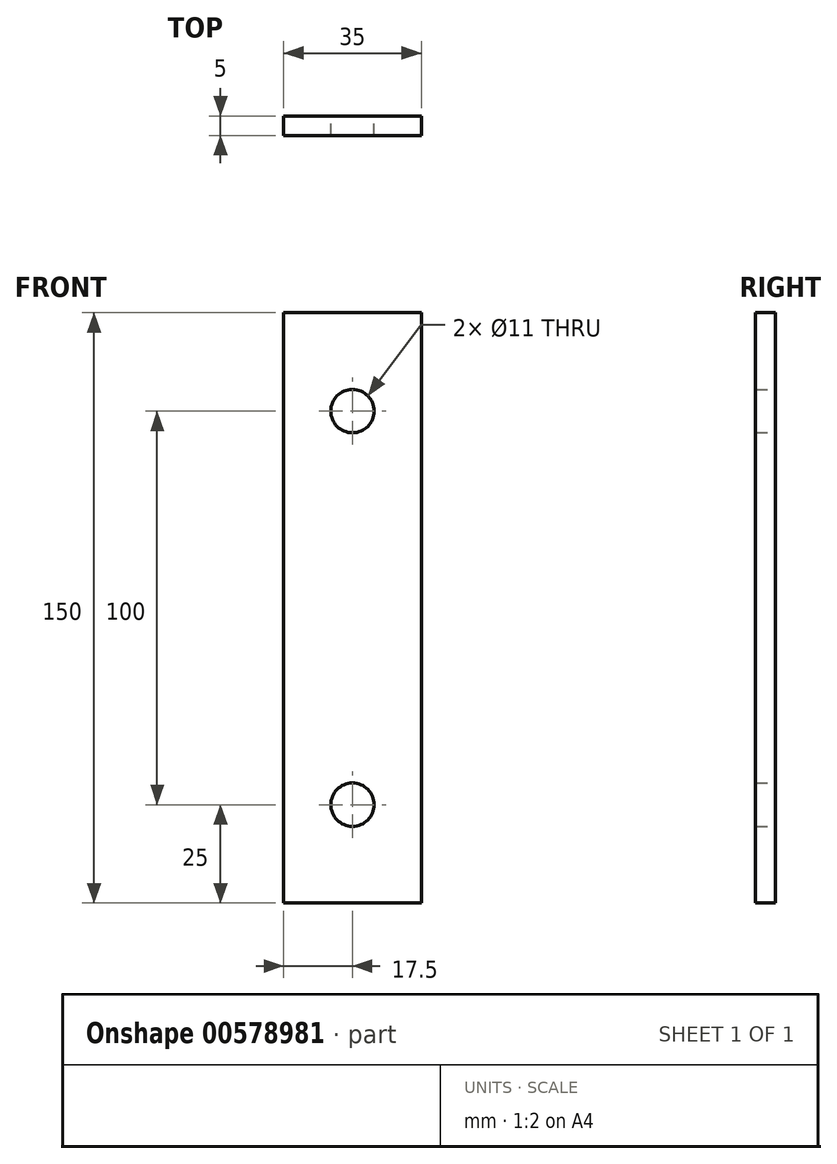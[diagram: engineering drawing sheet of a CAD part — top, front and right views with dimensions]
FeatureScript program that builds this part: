
annotation { "Feature Type Name" : "Feature", "Feature Type Description" : "" }
export const myFeature = defineFeature(function(context is Context, id is Id, definition is map)
    precondition{}
    {
        {
            var Q0;
            Q0=qCreatedBy(makeId("Front.planeOp"),FACE);
            var sketch = newSketch(context, id + "F0", { "sketchPlane" : qUnion([Q0])});
            skLineSegment(sketch, "E0.bottom", {"start": v(17.5, 75) * mm, "end": v(-17.5, 75) * mm});
            skLineSegment(sketch, "E0.top", {"start": v(17.5, -75) * mm, "end": v(-17.5, -75) * mm});
            skLineSegment(sketch, "E0.left", {"start": v(17.5, 75) * mm, "end": v(17.5, -75) * mm});
            skLineSegment(sketch, "E0.right", {"start": v(-17.5, 75) * mm, "end": v(-17.5, -75) * mm});
            skPoint(sketch, "E0.middle", {"position": v(0, 0) * mm});
            skCircle(sketch, "E1", {"center": v(0, -50) * mm, "radius": 5.5 * mm});
            skPoint(sketch, "E1.centerSnap0", {"position": v(0, -75) * mm});
            skCircle(sketch, "E2", {"center": v(0, 50) * mm, "radius": 5.5 * mm});
            skSolve(sketch);
        }
        {
            var Q0;
            Q0=makeQuery(id+"F0.imprint","IMPRINT",FACE,{"disambiguationData":[TD([[makeQuery(id+"F0.imprint","IMPRINT",EDGE,{"derivedFrom":sQuery(id+"F0.wireOp",EDGE,"E0.bottom")}),1.0]])]});
            extrude(context, id + "F1", {"entities" : qUnion([Q0]), "endBound" : BoundingType.SYMMETRIC, "depth" : 5 * mm, "offsetDistance" : 25 * mm});
        }
    });
